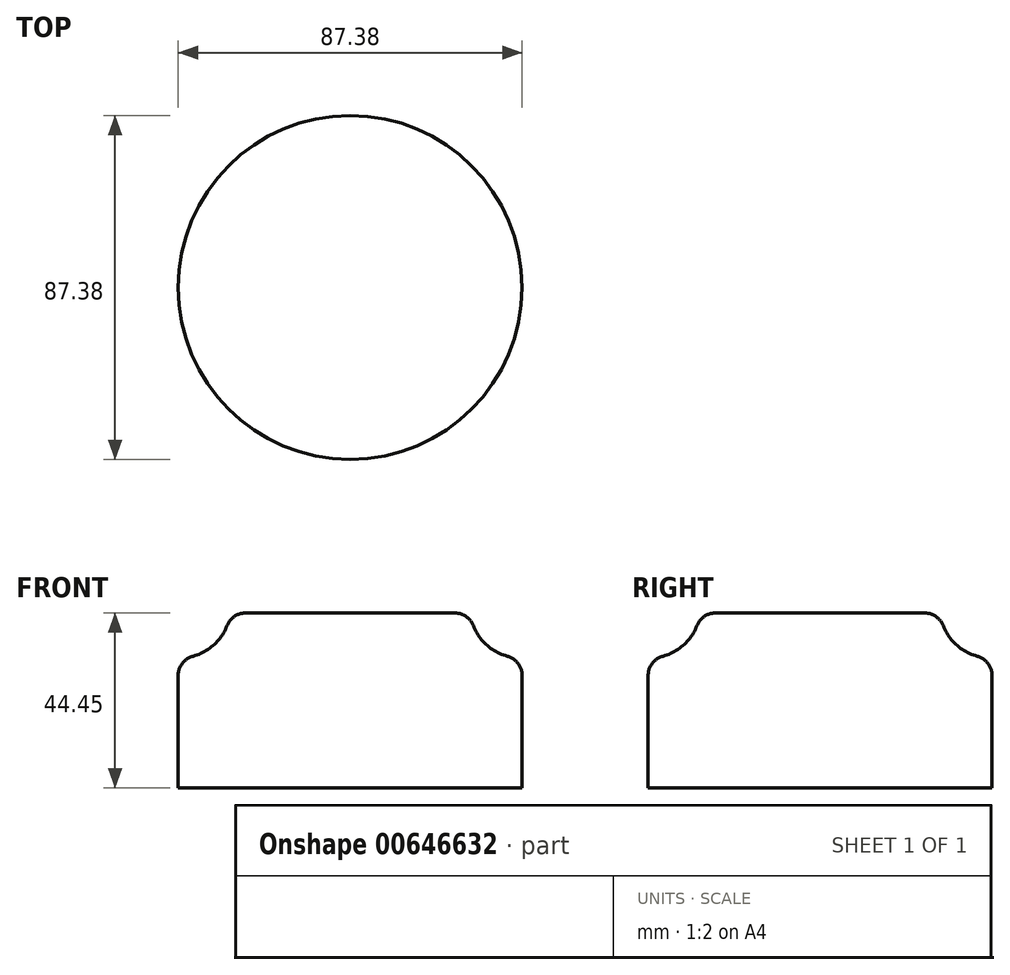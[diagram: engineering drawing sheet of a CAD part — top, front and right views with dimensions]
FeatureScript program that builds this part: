
annotation { "Feature Type Name" : "Feature", "Feature Type Description" : "" }
export const myFeature = defineFeature(function(context is Context, id is Id, definition is map)
    precondition{}
    {
        {
            var Q0;
            Q0=qCreatedBy(makeId("Front.planeOp"),FACE);
            var sketch = newSketch(context, id + "F0", { "sketchPlane" : qUnion([Q0])});
            skLineSegment(sketch, "E0", {"start": v(0, 18.06) * mm, "end": v(0, -26.39) * mm});
            skLineSegment(sketch, "E1", {"start": v(0, -26.39) * mm, "end": v(43.69, -26.39) * mm});
            skLineSegment(sketch, "E2", {"start": v(0, 18.06) * mm, "end": v(30.48, 18.06) * mm});
            skLineSegment(sketch, "E3", {"start": v(43.69, -26.39) * mm, "end": v(43.69, 6.63) * mm});
            skArc(sketch, "E4", {"start": v(30.48, 18.06) * mm, "mid": v(34.86, 9.78) * mm, "end": v(43.69, 6.63) * mm});
            skSolve(sketch);
        }
        {
            var Q0;
            Q0=qCreatedBy(makeId("Front.planeOp"),FACE);
            var sketch = newSketch(context, id + "F1", { "sketchPlane" : qUnion([Q0])});
            skLineSegment(sketch, "E5", {"start": v(0, -38.42) * mm, "end": v(0, -60.3) * mm});
            skSolve(sketch);
        }
        {
            var Q0;
            Q0=makeQuery(id+"F0.imprint","IMPRINT",FACE,{"disambiguationData":[TD([[makeQuery(id+"F0.imprint","IMPRINT",EDGE,{"derivedFrom":sQuery(id+"F0.wireOp",EDGE,"E0")}),1.0]])]});
            var Q1;
            Q1=sQuery(id+"F1.wireOp",EDGE,"E5");
            revolve(context, id + "F2", {"entities" : qUnion([Q0]), "axis" : qUnion([Q1]), "revolveType" : RevolveType.FULL});
        }
        {
            var Q0;
            Q0=makeQuery(id+"F2.opRevolve","SWEPT_EDGE",EDGE,{"disambiguationData":[OSD([sQuery(id+"F0.wireOp",EDGE,"E2"),sQuery(id+"F0.wireOp",EDGE,"bANWsTO2-NIDf-5Cpl-dMYv-VGzSQwf5gpid")])]});
            fillet(context, id + "F3", {"entities" : qUnion([Q0]), "radius" : 5.08 * mm, "tangentPropagation" : true, "allowEdgeOverflow" : false});
        }
        {
            var Q0;
            Q0=makeQuery(id+"F2.opRevolve","SWEPT_EDGE",EDGE,{"disambiguationData":[OSD([sQuery(id+"F0.wireOp",EDGE,"E3"),sQuery(id+"F0.wireOp",EDGE,"E4")])]});
            fillet(context, id + "F4", {"entities" : qUnion([Q0]), "radius" : 5.08 * mm, "tangentPropagation" : true, "allowEdgeOverflow" : false});
        }
    });
